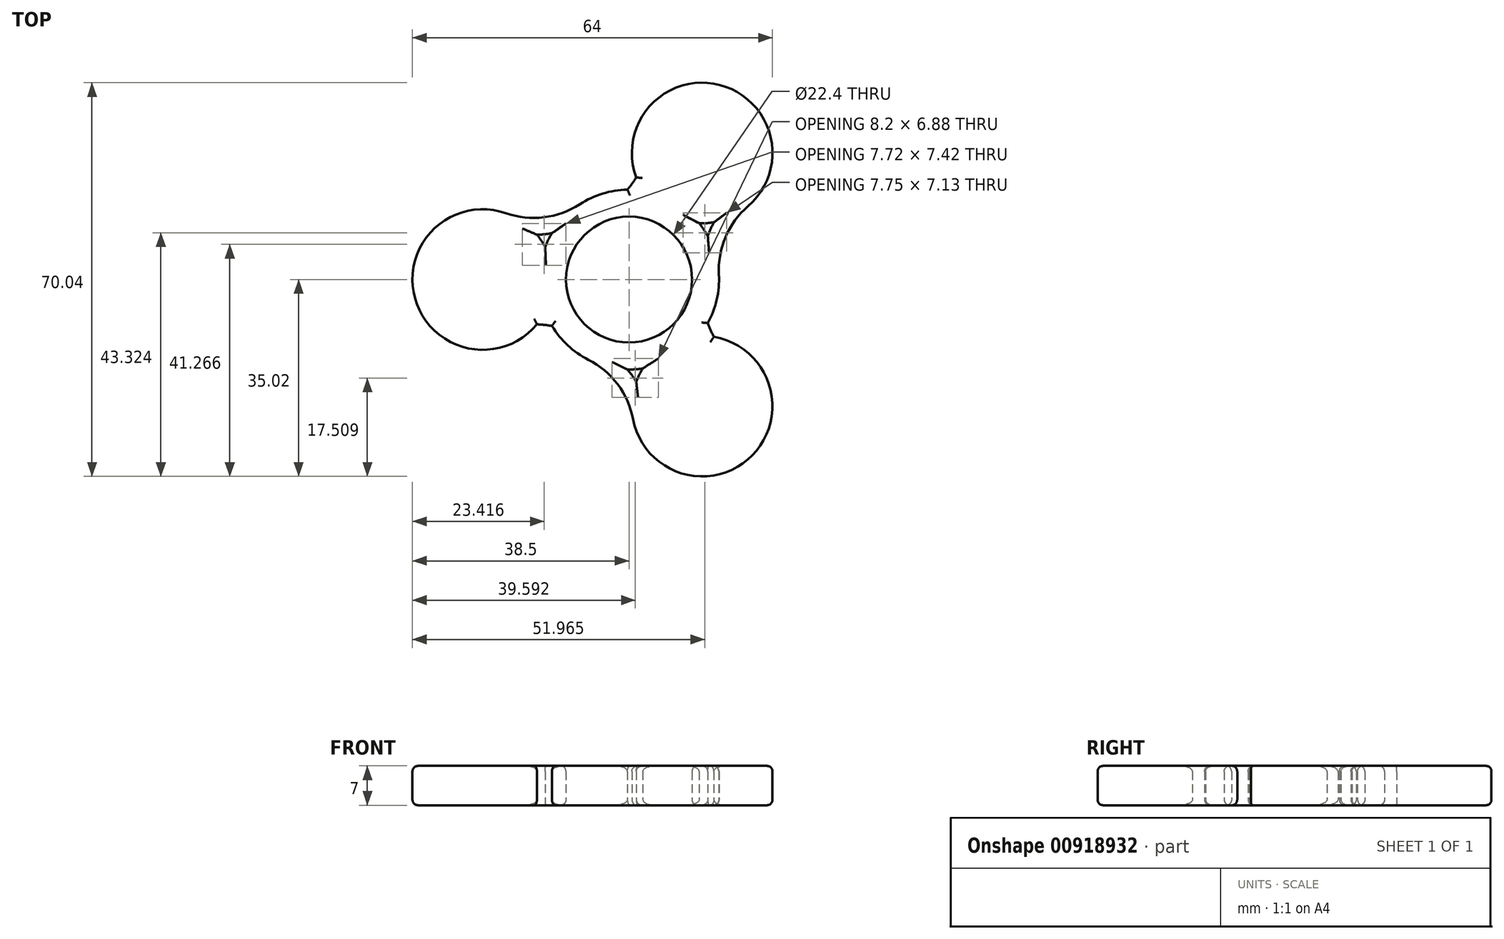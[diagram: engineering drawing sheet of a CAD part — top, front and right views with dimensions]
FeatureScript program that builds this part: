
annotation { "Feature Type Name" : "Feature", "Feature Type Description" : "" }
export const myFeature = defineFeature(function(context is Context, id is Id, definition is map)
    precondition{}
    {
        {
            var Q0;
            Q0=qCreatedBy(makeId("Top.planeOp"),FACE);
            var sketch = newSketch(context, id + "F0", { "sketchPlane" : qUnion([Q0])});
            skCircle(sketch, "E0", {"center": v(0, 0) * mm, "radius": 11.2 * mm});
            skCircle(sketch, "E1", {"center": v(0, 0) * mm, "radius": 16 * mm});
            skLineSegment(sketch, "E2", {"start": v(0, 0) * mm, "end": v(-26, 0) * mm, "construction": true});
            skCircle(sketch, "E3", {"center": v(-26, 0) * mm, "radius": 12.5 * mm});
            skArc(sketch, "E4", {"start": v(-21.88, 11.8) * mm, "mid": v(-15.13, 11.07) * mm, "end": v(-8.74, 13.4) * mm});
            skArc(sketch, "E5", {"start": v(-16.37, 7.97) * mm, "mid": v(-15.03, 8.06) * mm, "end": v(-13.7, 8.26) * mm});
            skArc(sketch, "E6.MirrorCS", {"start": v(-16.37, -7.97) * mm, "mid": v(-15.03, -8.06) * mm, "end": v(-13.7, -8.26) * mm});
            skArc(sketch, "E7.MirrorCS", {"start": v(-21.88, -11.8) * mm, "mid": v(-15.13, -11.07) * mm, "end": v(-8.74, -13.4) * mm});
            skLineSegment(sketch, "E8.1.0", {"start": v(0, 0) * mm, "end": v(13, -22.52) * mm, "construction": true});
            skCircle(sketch, "E8.1.1", {"center": v(13, -22.52) * mm, "radius": 12.5 * mm});
            skArc(sketch, "E8.1.2", {"start": v(0.72, -24.85) * mm, "mid": v(-2.03, -18.64) * mm, "end": v(-7.23, -14.27) * mm});
            skArc(sketch, "E8.1.3", {"start": v(1.28, -18.17) * mm, "mid": v(0.53, -17.05) * mm, "end": v(-0.3, -16) * mm});
            skArc(sketch, "E8.1.4", {"start": v(15.1, -10.2) * mm, "mid": v(14.5, -8.99) * mm, "end": v(14, -7.74) * mm});
            skArc(sketch, "E8.1.5", {"start": v(21.16, -13.05) * mm, "mid": v(17.15, -7.56) * mm, "end": v(15.98, -0.87) * mm});
            skLineSegment(sketch, "E8.2.0", {"start": v(0, 0) * mm, "end": v(13, 22.52) * mm, "construction": true});
            skCircle(sketch, "E8.2.1", {"center": v(13, 22.52) * mm, "radius": 12.5 * mm});
            skArc(sketch, "E8.2.2", {"start": v(21.16, 13.05) * mm, "mid": v(17.15, 7.56) * mm, "end": v(15.98, 0.87) * mm});
            skArc(sketch, "E8.2.3", {"start": v(15.1, 10.2) * mm, "mid": v(14.5, 8.99) * mm, "end": v(14, 7.74) * mm});
            skArc(sketch, "E8.2.4", {"start": v(1.28, 18.17) * mm, "mid": v(0.53, 17.05) * mm, "end": v(-0.3, 16) * mm});
            skArc(sketch, "E8.2.5", {"start": v(0.72, 24.85) * mm, "mid": v(-2.03, 18.64) * mm, "end": v(-7.23, 14.27) * mm});
            skSolve(sketch);
        }
        {
            var Q0;
            {var subQ0=sQuery(id+"F0.wireOp",EDGE,"E3");var subQ4=sQuery(id+"F0.wireOp",EDGE,"E1");var subQ5=makeQuery(id+"F0.imprint","INTERSECT",VERTEX,{"disambiguationData":[OD(0.0)],"derivedFrom":[subQ4,subQ0]});Q0=makeQuery(id+"F0.imprint","IMPRINT",FACE,{"disambiguationData":[TD([[makeQuery(id+"F0.imprint","IMPRINT",EDGE,{"disambiguationData":[TD([[subQ5,-1.0]])],"derivedFrom":subQ4}),-1.0]])]});}
            var Q1;
            {var subQ0=sQuery(id+"F0.wireOp",EDGE,"E3");var subQ1=sQuery(id+"F0.wireOp",EDGE,"E1");var subQ2=makeQuery(id+"F0.imprint","INTERSECT",VERTEX,{"disambiguationData":[OD(0.0)],"derivedFrom":[subQ1,subQ0]});Q1=makeQuery(id+"F0.imprint","IMPRINT",FACE,{"disambiguationData":[TD([[makeQuery(id+"F0.imprint","IMPRINT",EDGE,{"disambiguationData":[TD([[subQ2,-1.0]])],"derivedFrom":subQ1}),1.0]])]});}
            var Q2;
            Q2=makeQuery(id+"F0.imprint","IMPRINT",FACE,{"disambiguationData":[TD([[makeQuery(id+"F0.imprint","IMPRINT",EDGE,{"derivedFrom":sQuery(id+"F0.wireOp",EDGE,"E0")}),-1.0]])]});
            var Q3;
            {var subQ0=sQuery(id+"F0.wireOp",EDGE,"E4");Q3=makeQuery(id+"F0.imprint","IMPRINT",FACE,{"disambiguationData":[TD([[makeQuery(id+"F0.imprint","IMPRINT",EDGE,{"derivedFrom":subQ0}),-1.0]])]});}
            var Q4;
            {var subQ0=sQuery(id+"F0.wireOp",EDGE,"E8.2.4");Q4=makeQuery(id+"F0.imprint","IMPRINT",FACE,{"disambiguationData":[TD([[makeQuery(id+"F0.imprint","IMPRINT",EDGE,{"derivedFrom":subQ0}),-1.0]])]});}
            var Q5;
            {var subQ0=sQuery(id+"F0.wireOp",EDGE,"E8.2.1");var subQ4=sQuery(id+"F0.wireOp",EDGE,"E1");var subQ5=makeQuery(id+"F0.imprint","INTERSECT",VERTEX,{"disambiguationData":[OD(0.0)],"derivedFrom":[subQ4,subQ0]});Q5=makeQuery(id+"F0.imprint","IMPRINT",FACE,{"disambiguationData":[TD([[makeQuery(id+"F0.imprint","IMPRINT",EDGE,{"disambiguationData":[TD([[subQ5,-1.0]])],"derivedFrom":subQ4}),-1.0]])]});}
            var Q6;
            {var subQ0=sQuery(id+"F0.wireOp",EDGE,"E8.2.1");var subQ1=sQuery(id+"F0.wireOp",EDGE,"E1");var subQ2=makeQuery(id+"F0.imprint","INTERSECT",VERTEX,{"disambiguationData":[OD(0.0)],"derivedFrom":[subQ1,subQ0]});Q6=makeQuery(id+"F0.imprint","IMPRINT",FACE,{"disambiguationData":[TD([[makeQuery(id+"F0.imprint","IMPRINT",EDGE,{"disambiguationData":[TD([[subQ2,-1.0]])],"derivedFrom":subQ1}),1.0]])]});}
            var Q7;
            {var subQ0=sQuery(id+"F0.wireOp",EDGE,"E8.2.2");Q7=makeQuery(id+"F0.imprint","IMPRINT",FACE,{"disambiguationData":[TD([[makeQuery(id+"F0.imprint","IMPRINT",EDGE,{"derivedFrom":subQ0}),-1.0]])]});}
            var Q8;
            {var subQ0=sQuery(id+"F0.wireOp",EDGE,"E8.1.4");Q8=makeQuery(id+"F0.imprint","IMPRINT",FACE,{"disambiguationData":[TD([[makeQuery(id+"F0.imprint","IMPRINT",EDGE,{"derivedFrom":subQ0}),-1.0]])]});}
            var Q9;
            {var subQ0=sQuery(id+"F0.wireOp",EDGE,"E8.1.1");var subQ4=sQuery(id+"F0.wireOp",EDGE,"E1");var subQ5=makeQuery(id+"F0.imprint","INTERSECT",VERTEX,{"disambiguationData":[OD(0.0)],"derivedFrom":[subQ4,subQ0]});Q9=makeQuery(id+"F0.imprint","IMPRINT",FACE,{"disambiguationData":[TD([[makeQuery(id+"F0.imprint","IMPRINT",EDGE,{"disambiguationData":[TD([[subQ5,-1.0]])],"derivedFrom":subQ4}),-1.0]])]});}
            var Q10;
            {var subQ0=sQuery(id+"F0.wireOp",EDGE,"E8.1.1");var subQ1=sQuery(id+"F0.wireOp",EDGE,"E1");var subQ2=makeQuery(id+"F0.imprint","INTERSECT",VERTEX,{"disambiguationData":[OD(0.0)],"derivedFrom":[subQ1,subQ0]});Q10=makeQuery(id+"F0.imprint","IMPRINT",FACE,{"disambiguationData":[TD([[makeQuery(id+"F0.imprint","IMPRINT",EDGE,{"disambiguationData":[TD([[subQ2,-1.0]])],"derivedFrom":subQ1}),1.0]])]});}
            var Q11;
            {var subQ0=sQuery(id+"F0.wireOp",EDGE,"E8.1.2");Q11=makeQuery(id+"F0.imprint","IMPRINT",FACE,{"disambiguationData":[TD([[makeQuery(id+"F0.imprint","IMPRINT",EDGE,{"derivedFrom":subQ0}),-1.0]])]});}
            var Q12;
            {var subQ0=sQuery(id+"F0.wireOp",EDGE,"E6.MirrorCS");Q12=makeQuery(id+"F0.imprint","IMPRINT",FACE,{"disambiguationData":[TD([[makeQuery(id+"F0.imprint","IMPRINT",EDGE,{"derivedFrom":subQ0}),-1.0]])]});}
            extrude(context, id + "F1", {"entities" : qUnion([Q0, Q1, Q2, Q3, Q4, Q5, Q6, Q7, Q8, Q9, Q10, Q11, Q12]), "depth" : 7 * mm, "offsetDistance" : 25 * mm});
        }
        {
            var Q0;
            Q0=makeQuery(id+"F1.opExtrude","CAP_FACE",FACE,{"disambiguationData":[OSD([sQuery(id+"F0.wireOp",EDGE,"E0"),sQuery(id+"F0.wireOp",EDGE,"E1"),sQuery(id+"F0.wireOp",EDGE,"E3"),sQuery(id+"F0.wireOp",EDGE,"E4"),sQuery(id+"F0.wireOp",EDGE,"E5"),sQuery(id+"F0.wireOp",EDGE,"E6.MirrorCS"),sQuery(id+"F0.wireOp",EDGE,"E7.MirrorCS"),sQuery(id+"F0.wireOp",EDGE,"E8.1.1"),sQuery(id+"F0.wireOp",EDGE,"E8.1.2"),sQuery(id+"F0.wireOp",EDGE,"E8.1.3"),sQuery(id+"F0.wireOp",EDGE,"E8.1.4"),sQuery(id+"F0.wireOp",EDGE,"E8.1.5"),sQuery(id+"F0.wireOp",EDGE,"E8.2.1"),sQuery(id+"F0.wireOp",EDGE,"E8.2.2"),sQuery(id+"F0.wireOp",EDGE,"E8.2.3"),sQuery(id+"F0.wireOp",EDGE,"E8.2.4"),sQuery(id+"F0.wireOp",EDGE,"E8.2.5")])],"isStart":false});
            var Q1;
            Q1=makeQuery(id+"F1.opExtrude","CAP_FACE",FACE,{"disambiguationData":[OSD([sQuery(id+"F0.wireOp",EDGE,"E0"),sQuery(id+"F0.wireOp",EDGE,"E1"),sQuery(id+"F0.wireOp",EDGE,"E3"),sQuery(id+"F0.wireOp",EDGE,"E4"),sQuery(id+"F0.wireOp",EDGE,"E5"),sQuery(id+"F0.wireOp",EDGE,"E6.MirrorCS"),sQuery(id+"F0.wireOp",EDGE,"E7.MirrorCS"),sQuery(id+"F0.wireOp",EDGE,"E8.1.1"),sQuery(id+"F0.wireOp",EDGE,"E8.1.2"),sQuery(id+"F0.wireOp",EDGE,"E8.1.3"),sQuery(id+"F0.wireOp",EDGE,"E8.1.4"),sQuery(id+"F0.wireOp",EDGE,"E8.1.5"),sQuery(id+"F0.wireOp",EDGE,"E8.2.1"),sQuery(id+"F0.wireOp",EDGE,"E8.2.2"),sQuery(id+"F0.wireOp",EDGE,"E8.2.3"),sQuery(id+"F0.wireOp",EDGE,"E8.2.4"),sQuery(id+"F0.wireOp",EDGE,"E8.2.5")])],"isStart":true});
            fillet(context, id + "F2", {"entities" : qUnion([Q0, Q1]), "radius" : 1 * mm, "tangentPropagation" : true, "allowEdgeOverflow" : false});
        }
    });
